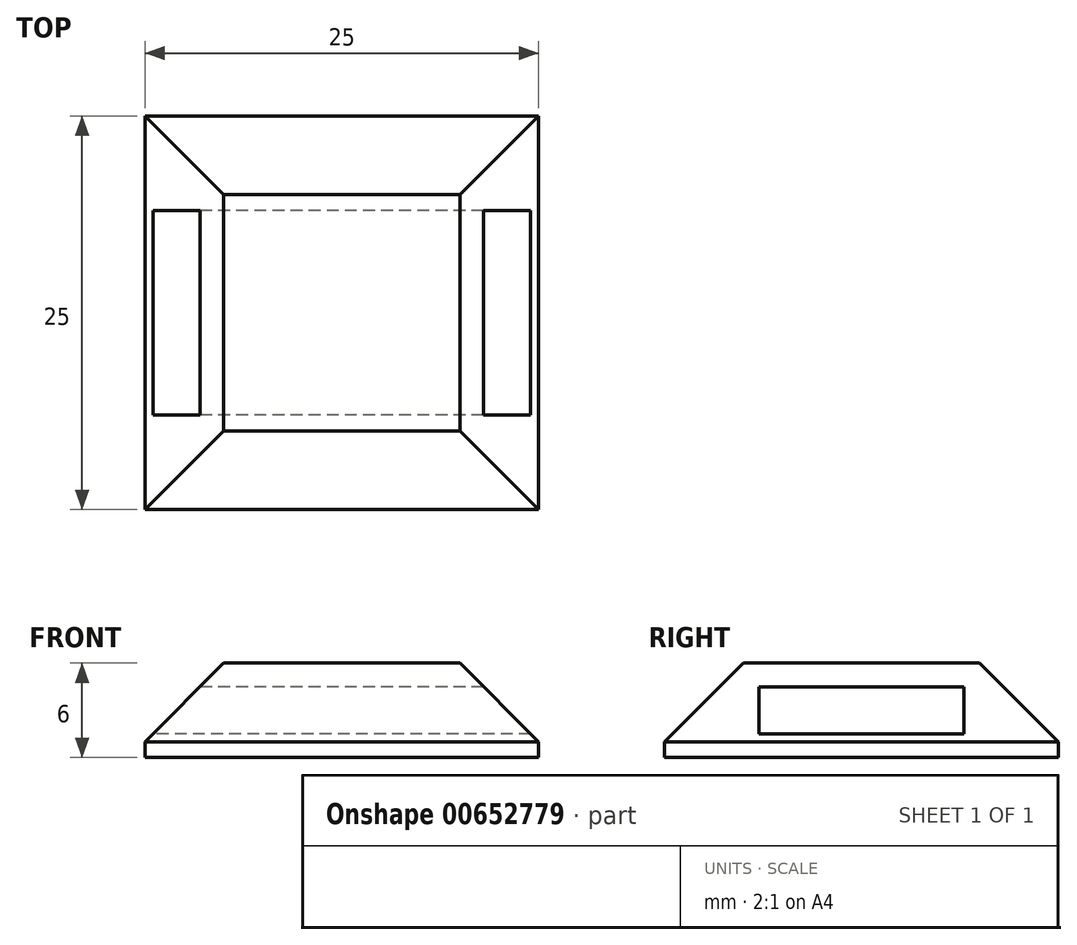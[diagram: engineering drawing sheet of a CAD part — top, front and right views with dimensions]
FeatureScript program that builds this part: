
annotation { "Feature Type Name" : "Feature", "Feature Type Description" : "" }
export const myFeature = defineFeature(function(context is Context, id is Id, definition is map)
    precondition{}
    {
        {
            var Q0;
            Q0=qCreatedBy(makeId("Top.planeOp"),FACE);
            var sketch = newSketch(context, id + "F0", { "sketchPlane" : qUnion([Q0])});
            skLineSegment(sketch, "E0.bottom", {"start": v(0, 0) * mm, "end": v(-25, 0) * mm});
            skLineSegment(sketch, "E0.top", {"start": v(0, 25) * mm, "end": v(-25, 25) * mm});
            skLineSegment(sketch, "E0.left", {"start": v(0, 0) * mm, "end": v(0, 25) * mm});
            skLineSegment(sketch, "E0.right", {"start": v(-25, 0) * mm, "end": v(-25, 25) * mm});
            skSolve(sketch);
        }
        {
            var Q0;
            Q0 = qSketchRegion(id + "F0", true);
            extrude(context, id + "F1", {"entities" : qUnion([Q0]), "depth" : 6 * mm, "offsetDistance" : 25 * mm});
        }
        {
            var Q0;
            Q0=makeQuery(id+"F1.opExtrude","SWEPT_FACE",FACE,{"disambiguationData":[OSD([sQuery(id+"F0.wireOp",EDGE,"E0.right")])]});
            var sketch = newSketch(context, id + "F2", { "sketchPlane" : qUnion([Q0])});
            skLineSegment(sketch, "E1.bottom", {"start": v(-19, 4.5) * mm, "end": v(-6, 4.5) * mm});
            skLineSegment(sketch, "E1.top", {"start": v(-19, 1.5) * mm, "end": v(-6, 1.5) * mm});
            skLineSegment(sketch, "E1.left", {"start": v(-19, 4.5) * mm, "end": v(-19, 1.5) * mm});
            skLineSegment(sketch, "E1.right", {"start": v(-6, 4.5) * mm, "end": v(-6, 1.5) * mm});
            skSolve(sketch);
        }
        {
            var Q0;
            Q0 = qSketchRegion(id + "F2", true);
            extrude(context, id + "F3", {"entities" : qUnion([Q0]), "operationType" : NewBodyOperationType.REMOVE, "oppositeDirection" : true, "depth" : 25 * mm, "offsetDistance" : 25 * mm});
        }
        {
            var Q0;
            Q0=makeQuery(id+"F1.opExtrude","CAP_EDGE",EDGE,{"disambiguationData":[OSD([sQuery(id+"F0.wireOp",EDGE,"E0.bottom")])],"isStart":false});
            var Q1;
            Q1=makeQuery(id+"F1.opExtrude","CAP_EDGE",EDGE,{"disambiguationData":[OSD([sQuery(id+"F0.wireOp",EDGE,"E0.right")])],"isStart":false});
            var Q2;
            Q2=makeQuery(id+"F1.opExtrude","CAP_EDGE",EDGE,{"disambiguationData":[OSD([sQuery(id+"F0.wireOp",EDGE,"E0.left")])],"isStart":false});
            var Q3;
            Q3=makeQuery(id+"F1.opExtrude","CAP_EDGE",EDGE,{"disambiguationData":[OSD([sQuery(id+"F0.wireOp",EDGE,"E0.top")])],"isStart":false});
            chamfer(context, id + "F4", {"entities" : qUnion([Q0, Q1, Q2, Q3]), "width" : 5 * mm, "tangentPropagation" : true});
        }
    });
